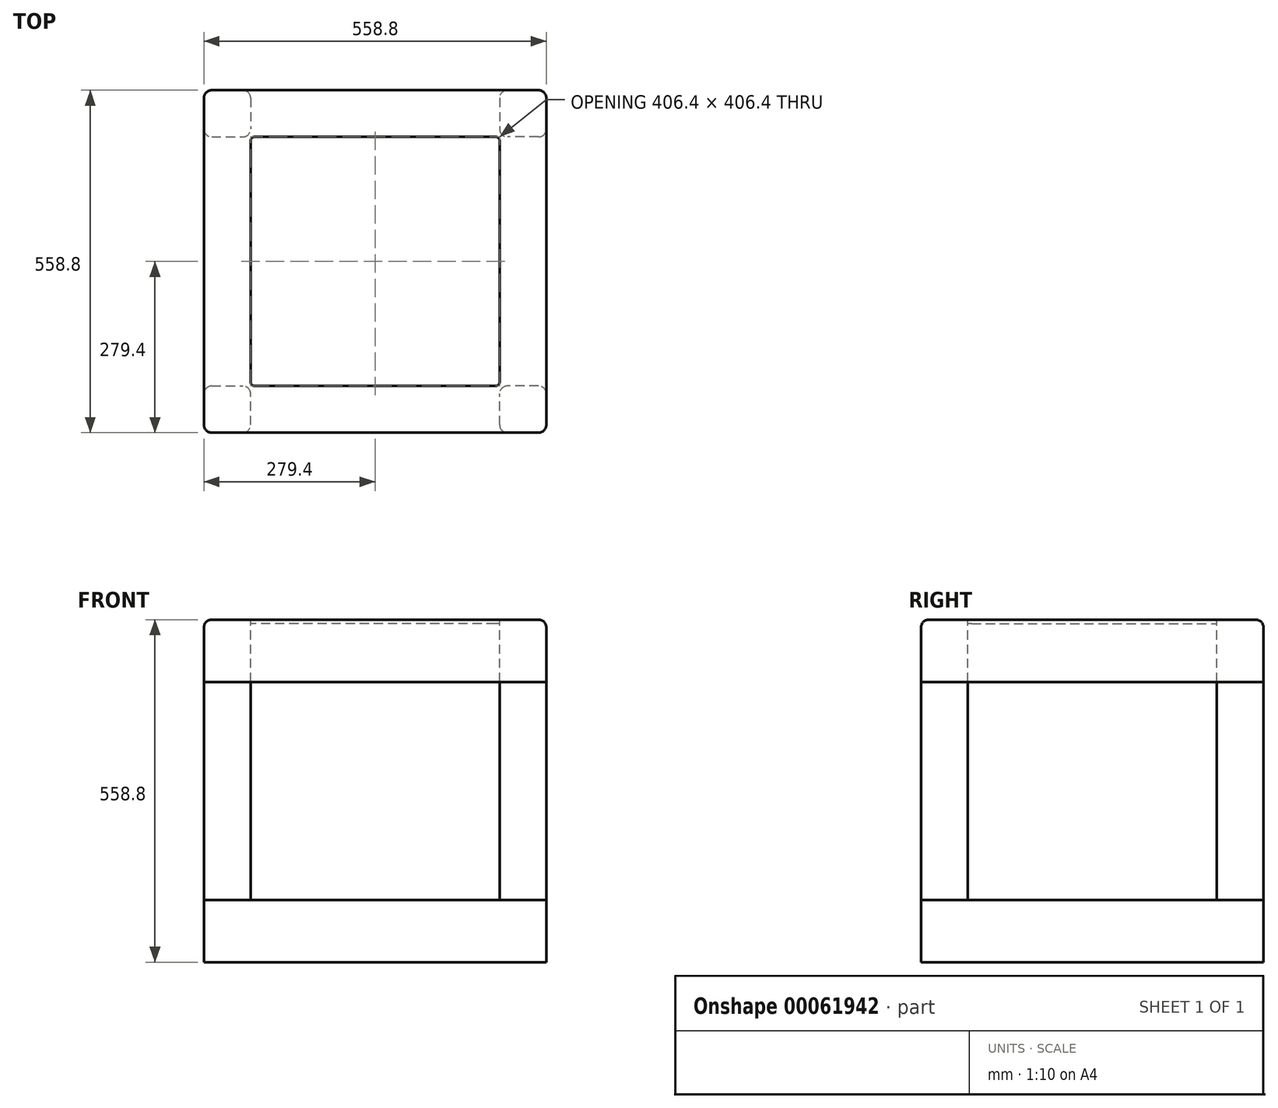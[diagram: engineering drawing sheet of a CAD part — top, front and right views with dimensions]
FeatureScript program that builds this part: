
annotation { "Feature Type Name" : "Feature", "Feature Type Description" : "" }
export const myFeature = defineFeature(function(context is Context, id is Id, definition is map)
    precondition{}
    {
        {
            var Q0;
            Q0=qCreatedBy(makeId("Front.planeOp"),FACE);
            var sketch = newSketch(context, id + "F0", { "sketchPlane" : qUnion([Q0])});
            skLineSegment(sketch, "E0.rect.bottom", {"start": v(279.4, -50.8) * mm, "end": v(-279.4, -50.8) * mm});
            skLineSegment(sketch, "E0.rect.top", {"start": v(279.4, 50.8) * mm, "end": v(-279.4, 50.8) * mm});
            skLineSegment(sketch, "E0.rect.left", {"start": v(279.4, -50.8) * mm, "end": v(279.4, 50.8) * mm});
            skLineSegment(sketch, "E0.rect.right", {"start": v(-279.4, -50.8) * mm, "end": v(-279.4, 50.8) * mm});
            skPoint(sketch, "E0.rect.middle", {"position": v(0, 0) * mm});
            skSolve(sketch);
        }
        {
            var Q0;
            Q0=makeQuery(id+"F0.imprint","IMPRINT",FACE,{"disambiguationData":[TD([[makeQuery(id+"F0.imprint","IMPRINT",EDGE,{"derivedFrom":sQuery(id+"F0.wireOp",EDGE,"E0.rect.bottom")}),-1.0]])]});
            extrude(context, id + "F1", {"entities" : qUnion([Q0]), "depth" : 558.8 * mm});
        }
        {
            var Q0;
            Q0=makeQuery(id+"F1.opExtrude","SWEPT_FACE",FACE,{"disambiguationData":[OSD([sQuery(id+"F0.wireOp",EDGE,"E0.rect.top")])]});
            var sketch = newSketch(context, id + "F2", { "sketchPlane" : qUnion([Q0])});
            skLineSegment(sketch, "E1.bottom", {"start": v(-279.4, -558.8) * mm, "end": v(-203.2, -558.8) * mm});
            skLineSegment(sketch, "E1.top", {"start": v(-279.4, -482.6) * mm, "end": v(-203.2, -482.6) * mm});
            skLineSegment(sketch, "E1.left", {"start": v(-279.4, -558.8) * mm, "end": v(-279.4, -482.6) * mm});
            skLineSegment(sketch, "E1.right", {"start": v(-203.2, -558.8) * mm, "end": v(-203.2, -482.6) * mm});
            skLineSegment(sketch, "E2", {"start": v(0, 0) * mm, "end": v(0, -558.8) * mm, "construction": true});
            skLineSegment(sketch, "E3", {"start": v(-279.4, -279.4) * mm, "end": v(279.4, -279.4) * mm, "construction": true});
            skLineSegment(sketch, "E4.MirrorCS", {"start": v(203.2, -558.8) * mm, "end": v(203.2, -482.6) * mm});
            skLineSegment(sketch, "E5.MirrorCS", {"start": v(279.4, -482.6) * mm, "end": v(203.2, -482.6) * mm});
            skLineSegment(sketch, "E6.MirrorCS", {"start": v(279.4, -558.8) * mm, "end": v(203.2, -558.8) * mm});
            skLineSegment(sketch, "E7.MirrorCS", {"start": v(279.4, -558.8) * mm, "end": v(279.4, -482.6) * mm});
            skLineSegment(sketch, "E8.MirrorCS", {"start": v(203.2, 0) * mm, "end": v(203.2, -76.2) * mm});
            skLineSegment(sketch, "E9.MirrorCS", {"start": v(279.4, -76.2) * mm, "end": v(203.2, -76.2) * mm});
            skLineSegment(sketch, "E10.MirrorCS", {"start": v(279.4, 0) * mm, "end": v(203.2, 0) * mm});
            skLineSegment(sketch, "E11.MirrorCS", {"start": v(-203.2, 0) * mm, "end": v(-203.2, -76.2) * mm});
            skLineSegment(sketch, "E12.MirrorCS", {"start": v(-279.4, 0) * mm, "end": v(-279.4, -76.2) * mm});
            skLineSegment(sketch, "E13.MirrorCS", {"start": v(279.4, 0) * mm, "end": v(279.4, -76.2) * mm});
            skLineSegment(sketch, "E14.MirrorCS", {"start": v(-279.4, -76.2) * mm, "end": v(-203.2, -76.2) * mm});
            skLineSegment(sketch, "E15.MirrorCS", {"start": v(-279.4, 0) * mm, "end": v(-203.2, 0) * mm});
            skSolve(sketch);
        }
        {
            var Q0;
            Q0=makeQuery(id+"F2.imprint","IMPRINT",FACE,{"disambiguationData":[TD([[makeQuery(id+"F2.imprint","IMPRINT",EDGE,{"derivedFrom":sQuery(id+"F2.wireOp",EDGE,"E11.MirrorCS")}),-1.0]])]});
            var Q1;
            Q1=makeQuery(id+"F2.imprint","IMPRINT",FACE,{"disambiguationData":[TD([[makeQuery(id+"F2.imprint","IMPRINT",EDGE,{"derivedFrom":sQuery(id+"F2.wireOp",EDGE,"E8.MirrorCS")}),1.0]])]});
            var Q2;
            Q2=makeQuery(id+"F2.imprint","IMPRINT",FACE,{"disambiguationData":[TD([[makeQuery(id+"F2.imprint","IMPRINT",EDGE,{"derivedFrom":sQuery(id+"F2.wireOp",EDGE,"E4.MirrorCS")}),-1.0]])]});
            var Q3;
            Q3=makeQuery(id+"F2.imprint","IMPRINT",FACE,{"disambiguationData":[TD([[makeQuery(id+"F2.imprint","IMPRINT",EDGE,{"derivedFrom":sQuery(id+"F2.wireOp",EDGE,"E1.bottom")}),-1.0]])]});
            extrude(context, id + "F3", {"entities" : qUnion([Q0, Q1, Q2, Q3]), "depth" : 355.6 * mm});
        }
        {
            var Q0;
            Q0=makeQuery(id+"F1.opExtrude","SWEPT_BODY",BODY,{"disambiguationData":[OSD([sQuery(id+"F0.wireOp",EDGE,"E0.rect.bottom"),sQuery(id+"F0.wireOp",EDGE,"E0.rect.top"),sQuery(id+"F0.wireOp",EDGE,"E0.rect.left"),sQuery(id+"F0.wireOp",EDGE,"E0.rect.right")])]});
            var Q1;
            Q1=makeQuery(id+"F3.opExtrude","SWEPT_EDGE",EDGE,{"disambiguationData":[OSD([sQuery(id+"F2.wireOp",EDGE,"E12.MirrorCS"),sQuery(id+"F2.wireOp",EDGE,"E15.MirrorCS")])]});
            var Q2;
            Q2=makeQuery(id+"F3.opExtrude","SWEPT_EDGE",EDGE,{"disambiguationData":[OSD([sQuery(id+"F0.wireOp",EDGE,"E0.rect.top"),sQuery(id+"F0.wireOp",EDGE,"E0.rect.right"),sQuery(id+"F2.wireOp",EDGE,"E12.MirrorCS"),sQuery(id+"F2.wireOp",EDGE,"E14.MirrorCS")])]});
            transform(context, id + "F4", {"entities" : qUnion([Q0]), "transformType" : TransformType.TRANSLATION_DISTANCE, "transformDirection" : qUnion([Q2]), "distance" : 457.2 * mm, "oppositeDirection" : true, "makeCopy" : true});
        }
        {
            var Q0;
            Q0=makeQuery(id+"F4.opPattern","COPY",FACE,{"derivedFrom":makeQuery(id+"F1.opExtrude","SWEPT_FACE",FACE,{"disambiguationData":[OSD([sQuery(id+"F0.wireOp",EDGE,"E0.rect.top")])]}),"instanceName":"1"});
            var sketch = newSketch(context, id + "F5", { "sketchPlane" : qUnion([Q0])});
            skLineSegment(sketch, "E16.rect.bottom", {"start": v(196.85, -482.6) * mm, "end": v(-196.85, -482.6) * mm});
            skLineSegment(sketch, "E16.rect.top", {"start": v(196.85, -76.2) * mm, "end": v(-196.85, -76.2) * mm});
            skLineSegment(sketch, "E16.rect.left", {"start": v(203.2, -476.25) * mm, "end": v(203.2, -82.55) * mm});
            skLineSegment(sketch, "E16.rect.right", {"start": v(-203.2, -476.25) * mm, "end": v(-203.2, -82.55) * mm});
            skPoint(sketch, "E16.rect.middle", {"position": v(0, -279.4) * mm});
            skPoint(sketch, "E16.rect.middle.positionSnap0", {"position": v(-279.4, -279.4) * mm});
            skPoint(sketch, "E16.rect.middle.positionSnap1", {"position": v(0, -558.8) * mm});
            skPoint(sketch, "E16.rect.centerSnap0", {"position": v(-279.4, -279.4) * mm});
            skPoint(sketch, "E16.rect.centerSnap1", {"position": v(0, -558.8) * mm});
            skPoint(sketch, "E17.visualSharp", {"position": v(-203.2, -76.2) * mm});
            skArc(sketch, "E17.filletArc", {"start": v(-196.85, -76.2) * mm, "mid": v(-201.34, -78.06) * mm, "end": v(-203.2, -82.55) * mm});
            skPoint(sketch, "E18.visualSharp", {"position": v(203.2, -76.2) * mm});
            skArc(sketch, "E18.filletArc", {"start": v(203.2, -82.55) * mm, "mid": v(201.34, -78.06) * mm, "end": v(196.85, -76.2) * mm});
            skPoint(sketch, "E19.visualSharp", {"position": v(203.2, -482.6) * mm});
            skArc(sketch, "E19.filletArc", {"start": v(196.85, -482.6) * mm, "mid": v(201.34, -480.74) * mm, "end": v(203.2, -476.25) * mm});
            skPoint(sketch, "E20.visualSharp", {"position": v(-203.2, -482.6) * mm});
            skArc(sketch, "E20.filletArc", {"start": v(-203.2, -476.25) * mm, "mid": v(-201.34, -480.74) * mm, "end": v(-196.85, -482.6) * mm});
            skSolve(sketch);
        }
        {
            var Q0;
            Q0=makeQuery(id+"F5.imprint","IMPRINT",FACE,{"disambiguationData":[TD([[makeQuery(id+"F5.imprint","IMPRINT",EDGE,{"derivedFrom":sQuery(id+"F5.wireOp",EDGE,"E16.rect.bottom")}),-1.0]])]});
            extrude(context, id + "F6", {"entities" : qUnion([Q0]), "operationType" : NewBodyOperationType.REMOVE, "oppositeDirection" : true, "depth" : 101.6 * mm});
        }
        {
            var Q0;
            Q0=makeQuery(id+"F3.opExtrude","SWEPT_EDGE",EDGE,{"disambiguationData":[OSD([sQuery(id+"F2.wireOp",EDGE,"E6.MirrorCS"),sQuery(id+"F2.wireOp",EDGE,"E7.MirrorCS")])]});
            var Q1;
            Q1=makeQuery(id+"F3.opExtrude","SWEPT_EDGE",EDGE,{"disambiguationData":[OSD([sQuery(id+"F0.wireOp",EDGE,"E0.rect.top"),sQuery(id+"F2.wireOp",EDGE,"E4.MirrorCS"),sQuery(id+"F2.wireOp",EDGE,"E6.MirrorCS")])]});
            var Q2;
            Q2=makeQuery(id+"F3.opExtrude","SWEPT_EDGE",EDGE,{"disambiguationData":[OSD([sQuery(id+"F2.wireOp",EDGE,"E1.bottom"),sQuery(id+"F2.wireOp",EDGE,"E1.left")])]});
            var Q3;
            Q3=makeQuery(id+"F3.opExtrude","SWEPT_EDGE",EDGE,{"disambiguationData":[OSD([sQuery(id+"F0.wireOp",EDGE,"E0.rect.top"),sQuery(id+"F2.wireOp",EDGE,"E1.bottom"),sQuery(id+"F2.wireOp",EDGE,"E1.right")])]});
            var Q4;
            Q4=makeQuery(id+"F1.opExtrude","CAP_EDGE",EDGE,{"disambiguationData":[OSD([sQuery(id+"F0.wireOp",EDGE,"E0.rect.right")])],"isStart":false});
            var Q5;
            Q5=makeQuery(id+"F4.opPattern","COPY",EDGE,{"derivedFrom":makeQuery(id+"F1.opExtrude","CAP_EDGE",EDGE,{"disambiguationData":[OSD([sQuery(id+"F0.wireOp",EDGE,"E0.rect.right")])],"isStart":false}),"instanceName":"1"});
            var Q6;
            Q6=makeQuery(id+"F1.opExtrude","CAP_EDGE",EDGE,{"disambiguationData":[OSD([sQuery(id+"F0.wireOp",EDGE,"E0.rect.left")])],"isStart":false});
            var Q7;
            Q7=makeQuery(id+"F4.opPattern","COPY",EDGE,{"derivedFrom":makeQuery(id+"F1.opExtrude","CAP_EDGE",EDGE,{"disambiguationData":[OSD([sQuery(id+"F0.wireOp",EDGE,"E0.rect.left")])],"isStart":false}),"instanceName":"1"});
            var Q8;
            Q8=makeQuery(id+"F4.opPattern","COPY",EDGE,{"derivedFrom":makeQuery(id+"F1.opExtrude","CAP_EDGE",EDGE,{"disambiguationData":[OSD([sQuery(id+"F0.wireOp",EDGE,"E0.rect.top")])],"isStart":false}),"instanceName":"1"});
            var Q9;
            Q9=makeQuery(id+"F3.opExtrude","SWEPT_EDGE",EDGE,{"disambiguationData":[OSD([sQuery(id+"F0.wireOp",EDGE,"E0.rect.top"),sQuery(id+"F0.wireOp",EDGE,"E0.rect.left"),sQuery(id+"F2.wireOp",EDGE,"E5.MirrorCS"),sQuery(id+"F2.wireOp",EDGE,"E7.MirrorCS")])]});
            var Q10;
            Q10=makeQuery(id+"F3.opExtrude","SWEPT_EDGE",EDGE,{"disambiguationData":[OSD([sQuery(id+"F0.wireOp",EDGE,"E0.rect.top"),sQuery(id+"F0.wireOp",EDGE,"E0.rect.left"),sQuery(id+"F2.wireOp",EDGE,"E9.MirrorCS"),sQuery(id+"F2.wireOp",EDGE,"E13.MirrorCS")])]});
            var Q11;
            Q11=makeQuery(id+"F3.opExtrude","SWEPT_EDGE",EDGE,{"disambiguationData":[OSD([sQuery(id+"F2.wireOp",EDGE,"E10.MirrorCS"),sQuery(id+"F2.wireOp",EDGE,"E13.MirrorCS")])]});
            var Q12;
            Q12=makeQuery(id+"F1.opExtrude","CAP_EDGE",EDGE,{"disambiguationData":[OSD([sQuery(id+"F0.wireOp",EDGE,"E0.rect.left")])],"isStart":true});
            var Q13;
            Q13=makeQuery(id+"F4.opPattern","COPY",EDGE,{"derivedFrom":makeQuery(id+"F1.opExtrude","SWEPT_EDGE",EDGE,{"disambiguationData":[OSD([sQuery(id+"F0.wireOp",EDGE,"E0.rect.top"),sQuery(id+"F0.wireOp",EDGE,"E0.rect.left")])]}),"instanceName":"1"});
            var Q14;
            Q14=makeQuery(id+"F3.opExtrude","SWEPT_EDGE",EDGE,{"disambiguationData":[OSD([sQuery(id+"F0.wireOp",EDGE,"E0.rect.top"),sQuery(id+"F2.wireOp",EDGE,"E8.MirrorCS"),sQuery(id+"F2.wireOp",EDGE,"E10.MirrorCS")])]});
            var Q15;
            Q15=makeQuery(id+"F3.opExtrude","SWEPT_EDGE",EDGE,{"disambiguationData":[OSD([sQuery(id+"F0.wireOp",EDGE,"E0.rect.top"),sQuery(id+"F2.wireOp",EDGE,"E11.MirrorCS"),sQuery(id+"F2.wireOp",EDGE,"E15.MirrorCS")])]});
            var Q16;
            Q16=makeQuery(id+"F3.opExtrude","SWEPT_EDGE",EDGE,{"disambiguationData":[OSD([sQuery(id+"F2.wireOp",EDGE,"E12.MirrorCS"),sQuery(id+"F2.wireOp",EDGE,"E15.MirrorCS")])]});
            var Q17;
            Q17=makeQuery(id+"F1.opExtrude","CAP_EDGE",EDGE,{"disambiguationData":[OSD([sQuery(id+"F0.wireOp",EDGE,"E0.rect.right")])],"isStart":true});
            var Q18;
            Q18=makeQuery(id+"F4.opPattern","COPY",EDGE,{"derivedFrom":makeQuery(id+"F1.opExtrude","CAP_EDGE",EDGE,{"disambiguationData":[OSD([sQuery(id+"F0.wireOp",EDGE,"E0.rect.top")])],"isStart":true}),"instanceName":"1"});
            var Q19;
            Q19=makeQuery(id+"F4.opPattern","COPY",EDGE,{"derivedFrom":makeQuery(id+"F1.opExtrude","CAP_EDGE",EDGE,{"disambiguationData":[OSD([sQuery(id+"F0.wireOp",EDGE,"E0.rect.left")])],"isStart":true}),"instanceName":"1"});
            var Q20;
            Q20=makeQuery(id+"F4.opPattern","COPY",EDGE,{"derivedFrom":makeQuery(id+"F1.opExtrude","CAP_EDGE",EDGE,{"disambiguationData":[OSD([sQuery(id+"F0.wireOp",EDGE,"E0.rect.right")])],"isStart":true}),"instanceName":"1"});
            var Q21;
            Q21=makeQuery(id+"F3.opExtrude","SWEPT_EDGE",EDGE,{"disambiguationData":[OSD([sQuery(id+"F0.wireOp",EDGE,"E0.rect.top"),sQuery(id+"F0.wireOp",EDGE,"E0.rect.right"),sQuery(id+"F2.wireOp",EDGE,"E12.MirrorCS"),sQuery(id+"F2.wireOp",EDGE,"E14.MirrorCS")])]});
            var Q22;
            Q22=makeQuery(id+"F3.opExtrude","SWEPT_EDGE",EDGE,{"disambiguationData":[OSD([sQuery(id+"F0.wireOp",EDGE,"E0.rect.top"),sQuery(id+"F0.wireOp",EDGE,"E0.rect.right"),sQuery(id+"F2.wireOp",EDGE,"E1.top"),sQuery(id+"F2.wireOp",EDGE,"E1.left")])]});
            var Q23;
            Q23=makeQuery(id+"F4.opPattern","COPY",EDGE,{"derivedFrom":makeQuery(id+"F1.opExtrude","SWEPT_EDGE",EDGE,{"disambiguationData":[OSD([sQuery(id+"F0.wireOp",EDGE,"E0.rect.top"),sQuery(id+"F0.wireOp",EDGE,"E0.rect.right")])]}),"instanceName":"1"});
            var Q24;
            Q24=makeQuery(id+"F3.opExtrude","SWEPT_EDGE",EDGE,{"disambiguationData":[OSD([sQuery(id+"F2.wireOp",EDGE,"E8.MirrorCS"),sQuery(id+"F2.wireOp",EDGE,"E9.MirrorCS")])]});
            var Q25;
            Q25=makeQuery(id+"F3.opExtrude","SWEPT_EDGE",EDGE,{"disambiguationData":[OSD([sQuery(id+"F2.wireOp",EDGE,"E11.MirrorCS"),sQuery(id+"F2.wireOp",EDGE,"E14.MirrorCS")])]});
            var Q26;
            Q26=makeQuery(id+"F3.opExtrude","SWEPT_EDGE",EDGE,{"disambiguationData":[OSD([sQuery(id+"F2.wireOp",EDGE,"E1.top"),sQuery(id+"F2.wireOp",EDGE,"E1.right")])]});
            var Q27;
            Q27=makeQuery(id+"F3.opExtrude","SWEPT_EDGE",EDGE,{"disambiguationData":[OSD([sQuery(id+"F2.wireOp",EDGE,"E4.MirrorCS"),sQuery(id+"F2.wireOp",EDGE,"E5.MirrorCS")])]});
            fillet(context, id + "F7", {"entities" : qUnion([Q0, Q1, Q2, Q3, Q4, Q5, Q6, Q7, Q8, Q9, Q10, Q11, Q12, Q13, Q14, Q15, Q16, Q17, Q18, Q19, Q20, Q21, Q22, Q23, Q24, Q25, Q26, Q27]), "radius" : 12.7 * mm, "tangentPropagation" : true, "allowEdgeOverflow" : false});
        }
        {
            var Q0;
            Q0=makeQuery(id+"F4.opPattern","COPY",FACE,{"derivedFrom":makeQuery(id+"F1.opExtrude","SWEPT_FACE",FACE,{"disambiguationData":[OSD([sQuery(id+"F0.wireOp",EDGE,"E0.rect.top")])]}),"instanceName":"1"});
            var sketch = newSketch(context, id + "F8", { "sketchPlane" : qUnion([Q0])});
            skLineSegment(sketch, "E21.bottom", {"start": v(-196.85, -482.6) * mm, "end": v(196.85, -482.6) * mm});
            skLineSegment(sketch, "E21.top", {"start": v(-196.85, -76.2) * mm, "end": v(196.85, -76.2) * mm});
            skLineSegment(sketch, "E21.left", {"start": v(-203.2, -476.25) * mm, "end": v(-203.2, -82.55) * mm});
            skLineSegment(sketch, "E21.right", {"start": v(203.2, -476.25) * mm, "end": v(203.2, -82.55) * mm});
            skPoint(sketch, "E22.visualSharp", {"position": v(-203.2, -76.2) * mm});
            skArc(sketch, "E22.filletArc", {"start": v(-196.85, -76.2) * mm, "mid": v(-201.34, -78.06) * mm, "end": v(-203.2, -82.55) * mm});
            skPoint(sketch, "E23.visualSharp", {"position": v(203.2, -76.2) * mm});
            skArc(sketch, "E23.filletArc", {"start": v(203.2, -82.55) * mm, "mid": v(201.34, -78.06) * mm, "end": v(196.85, -76.2) * mm});
            skPoint(sketch, "E24.visualSharp", {"position": v(203.2, -482.6) * mm});
            skArc(sketch, "E24.filletArc", {"start": v(196.85, -482.6) * mm, "mid": v(201.34, -480.74) * mm, "end": v(203.2, -476.25) * mm});
            skPoint(sketch, "E25.visualSharp", {"position": v(-203.2, -482.6) * mm});
            skArc(sketch, "E25.filletArc", {"start": v(-203.2, -476.25) * mm, "mid": v(-201.34, -480.74) * mm, "end": v(-196.85, -482.6) * mm});
            skSolve(sketch);
        }
        {
            var Q0;
            Q0=makeQuery(id+"F8.imprint","IMPRINT",FACE,{"disambiguationData":[TD([[makeQuery(id+"F8.imprint","IMPRINT",EDGE,{"derivedFrom":sQuery(id+"F8.wireOp",EDGE,"E21.bottom")}),-1.0]])]});
            extrude(context, id + "F9", {"entities" : qUnion([Q0]), "oppositeDirection" : true, "depth" : 6.35 * mm});
        }
    });
